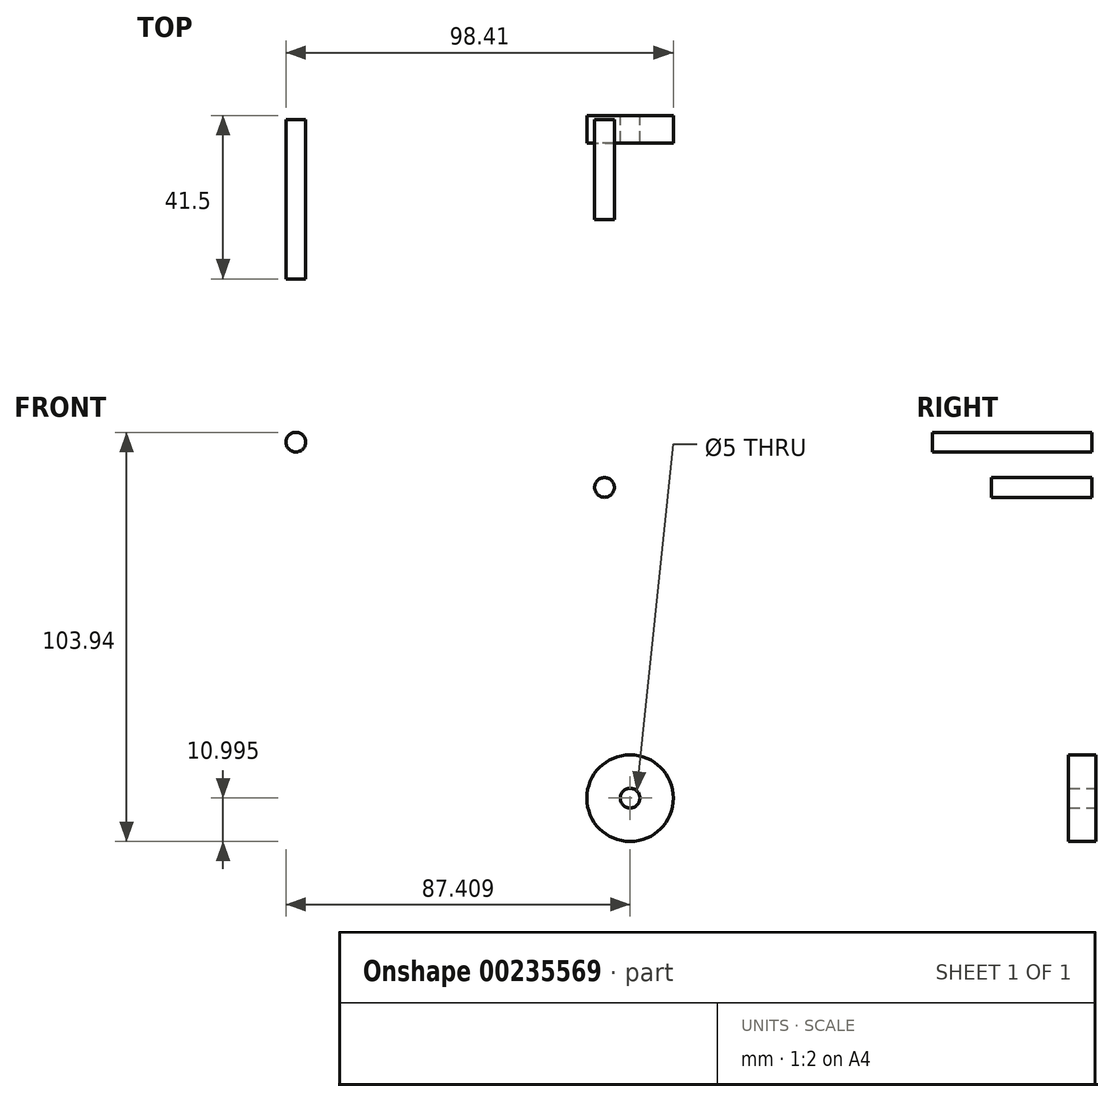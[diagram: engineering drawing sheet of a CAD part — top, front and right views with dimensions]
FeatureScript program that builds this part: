
annotation { "Feature Type Name" : "Feature", "Feature Type Description" : "" }
export const myFeature = defineFeature(function(context is Context, id is Id, definition is map)
    precondition{}
    {
        {
            var Q0;
            Q0=qCreatedBy(makeId("Front.planeOp"),FACE);
            var sketch = newSketch(context, id + "F0", { "sketchPlane" : qUnion([Q0])});
            skCircle(sketch, "E0", {"center": v(48.8, -46.8) * mm, "radius": 11 * mm});
            skCircle(sketch, "E1", {"center": v(48.8, -46.8) * mm, "radius": 2.5 * mm});
            skSolve(sketch);
        }
        {
            var Q0;
            Q0 = qSketchRegion(id + "F0", true);
            extrude(context, id + "F1", {"entities" : qUnion([Q0]), "depth" : 6 * mm, "hasSecondDirection" : true, "secondDirectionOppositeDirection" : true, "secondDirectionDepth" : 1 * mm});
        }
        {
            var Q0;
            Q0=qCreatedBy(makeId("Front.planeOp"),FACE);
            var sketch = newSketch(context, id + "F2", { "sketchPlane" : qUnion([Q0])});
            skCircle(sketch, "E2", {"center": v(42.3, 32.16) * mm, "radius": 2.5 * mm});
            skSolve(sketch);
        }
        {
            var Q0;
            Q0 = qSketchRegion(id + "F2", true);
            extrude(context, id + "F3", {"entities" : qUnion([Q0]), "depth" : 25.5 * mm});
        }
        {
            var Q0;
            Q0=qCreatedBy(makeId("Front.planeOp"),FACE);
            var sketch = newSketch(context, id + "F4", { "sketchPlane" : qUnion([Q0])});
            skCircle(sketch, "E3", {"center": v(-36.1, 43.65) * mm, "radius": 2.5 * mm});
            skSolve(sketch);
        }
        {
            var Q0;
            Q0 = qSketchRegion(id + "F4", true);
            extrude(context, id + "F5", {"entities" : qUnion([Q0]), "depth" : 40.5 * mm});
        }
    });
